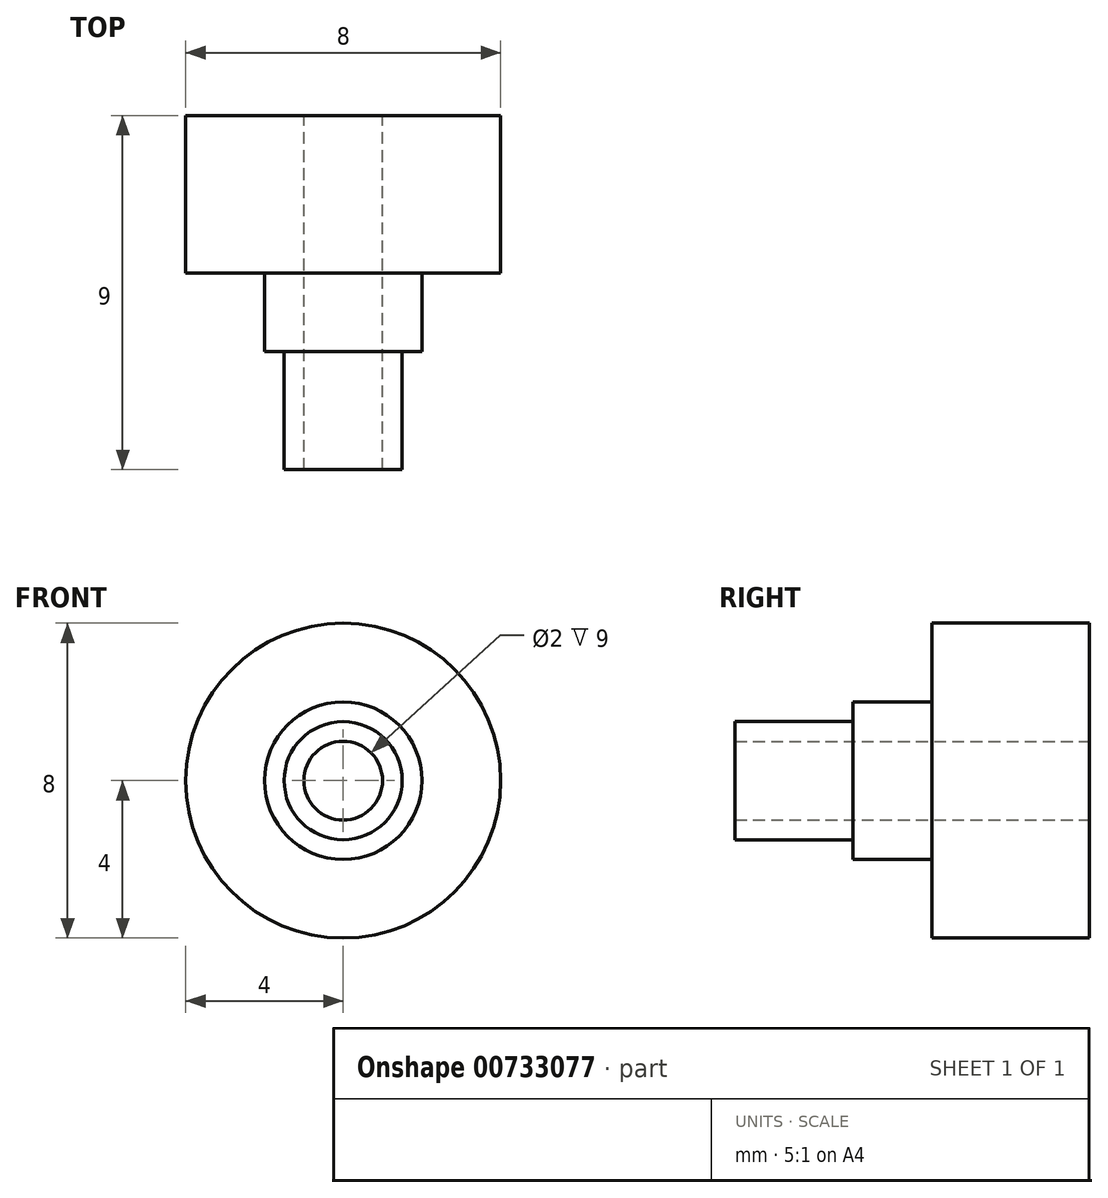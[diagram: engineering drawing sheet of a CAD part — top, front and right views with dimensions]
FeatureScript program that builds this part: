
annotation { "Feature Type Name" : "Feature", "Feature Type Description" : "" }
export const myFeature = defineFeature(function(context is Context, id is Id, definition is map)
    precondition{}
    {
        {
            var Q0;
            Q0=qCreatedBy(makeId("Right.planeOp"),FACE);
            var sketch = newSketch(context, id + "F0", { "sketchPlane" : qUnion([Q0])});
            skLineSegment(sketch, "E0", {"start": v(0, 0) * mm, "end": v(0, 4) * mm});
            skLineSegment(sketch, "E1", {"start": v(0, 4) * mm, "end": v(-4, 4) * mm});
            skLineSegment(sketch, "E2", {"start": v(-4, 4) * mm, "end": v(-4, 2) * mm});
            skLineSegment(sketch, "E3", {"start": v(-4, 2) * mm, "end": v(-6, 2) * mm});
            skLineSegment(sketch, "E4", {"start": v(-6, 2) * mm, "end": v(-6, 1.5) * mm});
            skLineSegment(sketch, "E5", {"start": v(-6, 1.5) * mm, "end": v(-9, 1.5) * mm});
            skLineSegment(sketch, "E6", {"start": v(-9, 1.5) * mm, "end": v(-9, 0) * mm});
            skLineSegment(sketch, "E7", {"start": v(-9, 0) * mm, "end": v(0, 0) * mm});
            skSolve(sketch);
        }
        {
            var Q0;
            Q0 = qSketchRegion(id + "F0", true);
            var Q1;
            Q1=sQuery(id+"F0.wireOp",EDGE,"E7");
            revolve(context, id + "F1", {"surfaceOperationType" : NewSurfaceOperationType.NEW, "entities" : qUnion([Q0]), "axis" : qUnion([Q1]), "revolveType" : RevolveType.FULL});
        }
        {
            var Q0;
            Q0=makeQuery(id+"F1.opRevolve","SWEPT_FACE",FACE,{"disambiguationData":[OSD([sQuery(id+"F0.wireOp",EDGE,"E0")])]});
            var sketch = newSketch(context, id + "F2", { "sketchPlane" : qUnion([Q0])});
            skCircle(sketch, "E8", {"center": v(0, 0) * mm, "radius": 1 * mm});
            skSolve(sketch);
        }
        {
            var Q0;
            Q0 = qSketchRegion(id + "F2", true);
            extrude(context, id + "F3", {"entities" : qUnion([Q0]), "operationType" : NewBodyOperationType.REMOVE, "endBound" : BoundingType.THROUGH_ALL, "oppositeDirection" : true, "depth" : 25 * mm, "offsetDistance" : 25 * mm});
        }
    });
